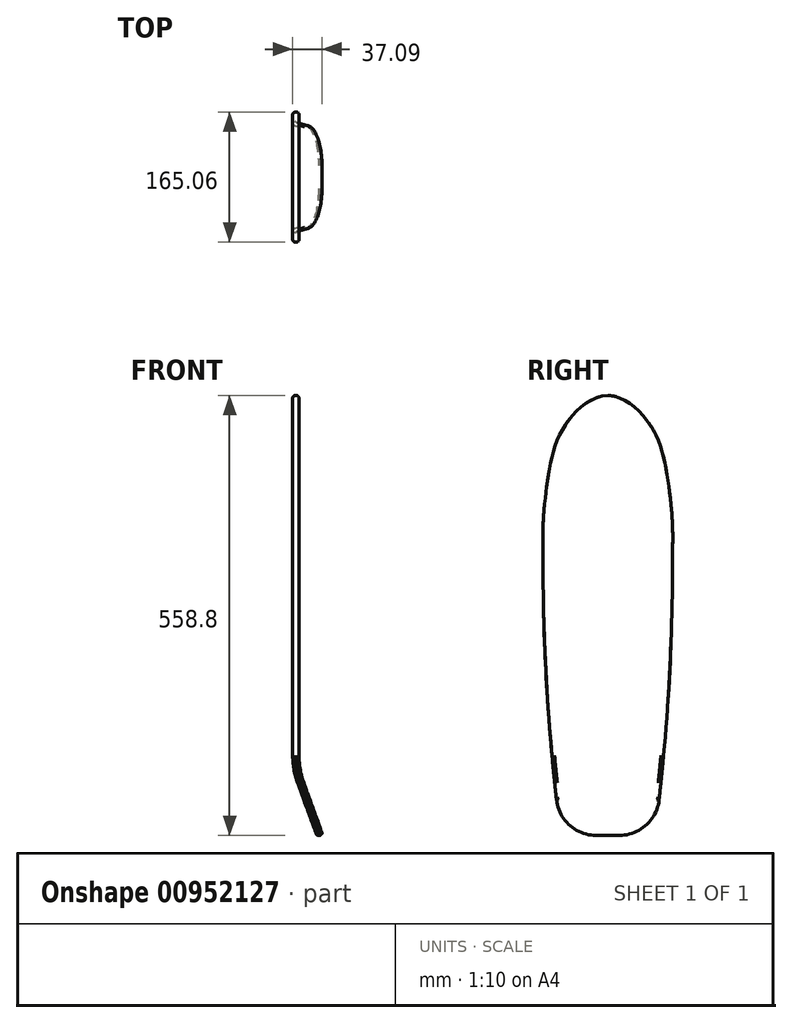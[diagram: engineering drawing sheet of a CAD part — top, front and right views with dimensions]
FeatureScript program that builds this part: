
annotation { "Feature Type Name" : "Feature", "Feature Type Description" : "" }
export const myFeature = defineFeature(function(context is Context, id is Id, definition is map)
    precondition{}
    {
        {
            var Q0;
            Q0=qCreatedBy(makeId("Front.planeOp"),FACE);
            var sketch = newSketch(context, id + "F0", { "sketchPlane" : qUnion([Q0])});
            skLineSegment(sketch, "E0", {"start": v(0, 279.4) * mm, "end": v(0, -279.4) * mm, "construction": true});
            skLineSegment(sketch, "E1", {"start": v(0, -195.58) * mm, "end": v(32.07, -283.7) * mm, "construction": true});
            skLineSegment(sketch, "E2.bottom", {"start": v(3.97, 279.4) * mm, "end": v(-3.97, 279.4) * mm});
            skLineSegment(sketch, "E2.top", {"start": v(3.97, -195.58) * mm, "end": v(-3.97, -195.58) * mm});
            skLineSegment(sketch, "E2.left", {"start": v(3.97, 279.4) * mm, "end": v(3.97, -195.58) * mm});
            skLineSegment(sketch, "E2.right", {"start": v(-3.97, 279.4) * mm, "end": v(-3.97, -195.58) * mm});
            skLineSegment(sketch, "E3", {"start": v(3.97, -195.58) * mm, "end": v(36.04, -283.7) * mm});
            skLineSegment(sketch, "E4", {"start": v(-3.97, -195.58) * mm, "end": v(29.03, -286.24) * mm});
            skLineSegment(sketch, "E5", {"start": v(29.03, -286.24) * mm, "end": v(36.04, -283.7) * mm});
            skSolve(sketch);
        }
        {
            var Q0;
            Q0 = qSketchRegion(id + "F0", true);
            extrude(context, id + "F1", {"entities" : qUnion([Q0]), "endBound" : BoundingType.SYMMETRIC, "depth" : 165.1 * mm, "offsetDistance" : 25.4 * mm});
        }
        {
            var Q0;
            Q0=qCreatedBy(makeId("Right.planeOp"),FACE);
            var sketch = newSketch(context, id + "F2", { "sketchPlane" : qUnion([Q0])});
            skLineSegment(sketch, "E6", {"start": v(0, 279.4) * mm, "end": v(0, -279.4) * mm, "construction": true});
            skLineSegment(sketch, "E7", {"start": v(-82.55, 119.74) * mm, "end": v(82.55, 119.74) * mm, "construction": true});
            skFitSpline(sketch, "E8", {"points": [v(0, 279.4) * mm, v(-53.98, 241.93) * mm, v(-82.55, 119.74) * mm], "startDerivative": vector(-148.08, 0) * mm, "endDerivative": vector(-33.05, -325.1) * mm});
            skFitSpline(sketch, "E9.MirrorCS", {"points": [v(0, 279.4) * mm, v(53.98, 241.93) * mm, v(82.55, 119.74) * mm], "startDerivative": vector(148.08, 0) * mm, "endDerivative": vector(33.05, -325.1) * mm});
            skLineSegment(sketch, "E10", {"start": v(-60.33, -279.4) * mm, "end": v(60.33, -279.4) * mm});
            skPoint(sketch, "E11.1.internal.snap0", {"position": v(-82.55, -49.94) * mm});
            skFitSpline(sketch, "E11", {"points": [v(-82.55, 119.74) * mm, v(-60.32, -279.4) * mm], "startDerivative": vector(0, -509.06) * mm, "endDerivative": vector(52.17, -470.82) * mm});
            skFitSpline(sketch, "E12.MirrorCS", {"points": [v(82.55, 119.74) * mm, v(60.33, -279.4) * mm], "startDerivative": vector(0, -509.06) * mm, "endDerivative": vector(-52.17, -470.82) * mm});
            skLineSegment(sketch, "E13.bottom", {"start": v(117.85, -295.93) * mm, "end": v(-131.18, -295.93) * mm});
            skLineSegment(sketch, "E13.top", {"start": v(117.85, 305.28) * mm, "end": v(-131.18, 305.28) * mm});
            skLineSegment(sketch, "E13.left", {"start": v(117.85, -295.93) * mm, "end": v(117.85, 305.28) * mm});
            skLineSegment(sketch, "E13.right", {"start": v(-131.18, -295.93) * mm, "end": v(-131.18, 305.28) * mm});
            skSolve(sketch);
        }
        {
            var Q0;
            Q0=makeQuery(id+"F2.imprint","IMPRINT",FACE,{"disambiguationData":[TD([[makeQuery(id+"F2.imprint","IMPRINT",EDGE,{"derivedFrom":sQuery(id+"F2.wireOp",EDGE,"E8")}),-1.0]])]});
            extrude(context, id + "F3", {"entities" : qUnion([Q0]), "operationType" : NewBodyOperationType.REMOVE, "endBound" : BoundingType.SYMMETRIC, "oppositeDirection" : true, "depth" : 101.6 * mm, "offsetDistance" : 25.4 * mm});
        }
        {
            var Q0;
            Q0=makeQuery(id+"F1.opExtrude","SWEPT_EDGE",EDGE,{"disambiguationData":[OSD([sQuery(id+"F0.wireOp",EDGE,"E2.top"),sQuery(id+"F0.wireOp",EDGE,"E2.right"),sQuery(id+"F0.wireOp",EDGE,"E4")])]});
            fillet(context, id + "F4", {"entities" : qUnion([Q0]), "radius" : 101.6 * mm, "tangentPropagation" : true, "allowEdgeOverflow" : false});
        }
        {
            var Q0;
            Q0=makeQuery(id+"F3.boolean.opBoolean","COPY",EDGE,{"derivedFrom":makeQuery(id+"F3.opExtrude","SWEPT_EDGE",EDGE,{"disambiguationData":[OSD([sQuery(id+"F2.wireOp",EDGE,"E8"),sQuery(id+"F2.wireOp",EDGE,"E11")])]})});
            var Q1;
            Q1=makeQuery(id+"F3.boolean.opBoolean","COPY",EDGE,{"derivedFrom":makeQuery(id+"F3.opExtrude","SWEPT_EDGE",EDGE,{"disambiguationData":[OSD([sQuery(id+"F2.wireOp",EDGE,"E9.MirrorCS"),sQuery(id+"F2.wireOp",EDGE,"E12.MirrorCS")])]})});
            fillet(context, id + "F5", {"entities" : qUnion([Q0, Q1]), "radius" : 381 * mm, "tangentPropagation" : true, "allowEdgeOverflow" : false});
        }
        {
            var Q0;
            Q0=makeQuery(id+"F1.opExtrude","SWEPT_EDGE",EDGE,{"disambiguationData":[OSD([sQuery(id+"F0.wireOp",EDGE,"E2.top"),sQuery(id+"F0.wireOp",EDGE,"E2.left"),sQuery(id+"F0.wireOp",EDGE,"E3")])]});
            fillet(context, id + "F6", {"entities" : qUnion([Q0]), "radius" : 101.6 * mm, "tangentPropagation" : true, "allowEdgeOverflow" : false});
        }
        {
            var Q0;
            Q0=makeQuery(id+"F3.boolean.opBoolean","COPY",EDGE,{"derivedFrom":makeQuery(id+"F3.opExtrude","SWEPT_EDGE",EDGE,{"disambiguationData":[OSD([sQuery(id+"F2.wireOp",EDGE,"E10"),sQuery(id+"F2.wireOp",EDGE,"E12.MirrorCS")])]})});
            var Q1;
            Q1=makeQuery(id+"F3.boolean.opBoolean","COPY",EDGE,{"derivedFrom":makeQuery(id+"F3.opExtrude","SWEPT_EDGE",EDGE,{"disambiguationData":[OSD([sQuery(id+"F2.wireOp",EDGE,"E10"),sQuery(id+"F2.wireOp",EDGE,"E11")])]})});
            fillet(context, id + "F7", {"entities" : qUnion([Q0, Q1]), "radius" : 50.8 * mm, "tangentPropagation" : true, "allowEdgeOverflow" : false});
        }
        {
            var Q0;
            Q0=makeQuery(id+"F1.opExtrude","SWEPT_FACE",FACE,{"disambiguationData":[OSD([sQuery(id+"F0.wireOp",EDGE,"E2.left")])]});
            var Q1;
            Q1=makeQuery(id+"F1.opExtrude","SWEPT_FACE",FACE,{"disambiguationData":[OSD([sQuery(id+"F0.wireOp",EDGE,"E3")])]});
            fillet(context, id + "F8", {"entities" : qUnion([Q0, Q1]), "radius" : 3.17 * mm, "tangentPropagation" : true, "allowEdgeOverflow" : false});
        }
        {
            var Q0;
            Q0=makeQuery(id+"F1.opExtrude","SWEPT_FACE",FACE,{"disambiguationData":[OSD([sQuery(id+"F0.wireOp",EDGE,"E2.right")])]});
            var Q1;
            Q1=makeQuery(id+"F1.opExtrude","SWEPT_FACE",FACE,{"disambiguationData":[OSD([sQuery(id+"F0.wireOp",EDGE,"E4")])]});
            var Q2;
            Q2=makeQuery(id+"F4.opFillet","BLEND_FACE",FACE,{"disambiguationData":[OSD([sQuery(id+"F0.wireOp",EDGE,"E2.top"),sQuery(id+"F0.wireOp",EDGE,"E2.right"),sQuery(id+"F0.wireOp",EDGE,"E4")])]});
            fillet(context, id + "F9", {"entities" : qUnion([Q0, Q1, Q2]), "radius" : 3.17 * mm, "tangentPropagation" : true, "allowEdgeOverflow" : false});
        }
    });
